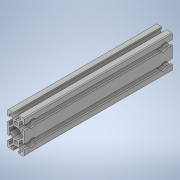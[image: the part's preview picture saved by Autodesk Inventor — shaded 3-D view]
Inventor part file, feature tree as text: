
AUTODESK INVENTOR PART (.ipt)
format: ipt  version: 2022 (Build 260153000, 153)  size: 366,080 bytes
history: native  units: mm
features: other x9, revolve x4, sketch x4, extrude x1, hole x1, pattern_linear x1
ambient origin geometry x8: Origin, YZ Plane, XZ Plane, XY Plane, X Axis, Y Axis, Z Axis, Center Point
bodies: Solid1 (feature_tree)
feature tree (20):
  extrude  "Extrusion1"  Depth=20.0mm TaperAngle=0.0deg
  hole  "Hole1"  [1 undecoded]
  pattern_linear  "Rectangular Pattern1"  Spacing1=360.0deg  [1 undecoded]
  revolve  "Revolution1"  [1 undecoded]
  revolve  "Revolution2"  [1 undecoded]
  revolve  "Revolution3"  [1 undecoded]
  revolve  "Revolution4"  [1 undecoded]
  other  "C1_XY"
  other  "C1_YZ"
  other  "C1_ZX"
  other  "C1_X"
  other  "C1_Y"
  other  "C1_Z"
  other  "C1_Center"
  sketch  "Sketch_1"  dims[d0=180.0mm d1=0.0mm]
  sketch  "Sketch2"  dims[d2=4.2mm d3=6.0mm d4=4.0mm d5=2.0mm d6=90.0deg d7=180.0mm d8=0.0mm d9=20.0mm d11=20.0mm d12=10.0mm d14=0.0mm]
  sketch  "Sketch_50"  dims[d15=360.0deg d16=360.0deg]
  other  "_p_______27_Sketch_50_0"
  sketch  "Sketch_51"  dims[d17=360.0deg d18=360.0deg d19=0.0mm]
  other  "_p_______28_Sketch_51_0"
note: 6 required parameter values undecoded (feature->parameter linkage not recoverable at this tier; creation-order binding heuristic only, values carry confidence <= 0.55)